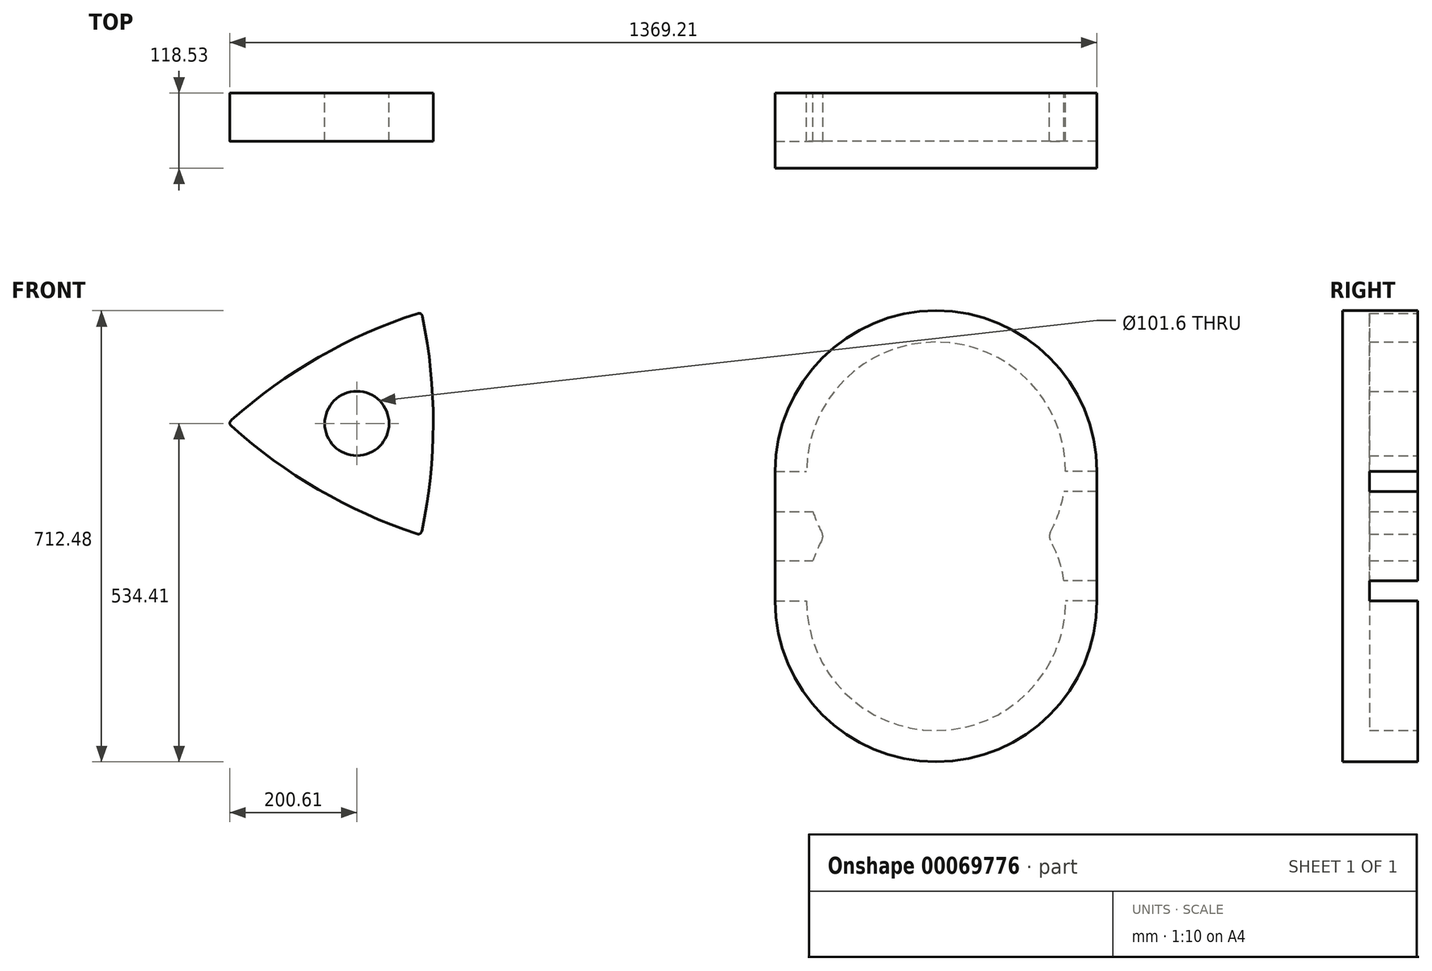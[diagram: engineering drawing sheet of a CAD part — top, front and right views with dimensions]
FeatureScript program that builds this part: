
annotation { "Feature Type Name" : "Feature", "Feature Type Description" : "" }
export const myFeature = defineFeature(function(context is Context, id is Id, definition is map)
    precondition{}
    {
        {
            var Q0;
            Q0=qCreatedBy(makeId("Front.planeOp"),FACE);
            var sketch = newSketch(context, id + "F0", { "sketchPlane" : qUnion([Q0])});
            skCircle(sketch, "E0", {"center": v(914.6, -75.93) * mm, "radius": 204.48 * mm});
            skCircle(sketch, "E1", {"center": v(914.6, -280.4) * mm, "radius": 204.48 * mm});
            skArc(sketch, "E2", {"start": v(1168.6, -75.93) * mm, "mid": v(914.6, 178.07) * mm, "end": v(660.6, -75.93) * mm});
            skLineSegment(sketch, "E3", {"start": v(660.6, -139.43) * mm, "end": v(660.6, -216.9) * mm});
            skArc(sketch, "E4", {"start": v(660.6, -280.4) * mm, "mid": v(914.6, -534.4) * mm, "end": v(1168.6, -280.4) * mm});
            skLineSegment(sketch, "E5", {"start": v(660.6, -75.93) * mm, "end": v(710.13, -75.93) * mm});
            skLineSegment(sketch, "E6", {"start": v(660.6, -139.43) * mm, "end": v(720.24, -139.43) * mm});
            skLineSegment(sketch, "E7", {"start": v(660.6, -216.9) * mm, "end": v(720.24, -216.9) * mm});
            skLineSegment(sketch, "E8", {"start": v(660.6, -280.4) * mm, "end": v(710.13, -280.4) * mm});
            skLineSegment(sketch, "E9", {"start": v(1168.6, -107.68) * mm, "end": v(1168.6, -248.66) * mm});
            skLineSegment(sketch, "E10", {"start": v(1168.6, -75.93) * mm, "end": v(1119.08, -75.93) * mm});
            skLineSegment(sketch, "E11", {"start": v(1168.6, -107.68) * mm, "end": v(1116.6, -107.68) * mm});
            skLineSegment(sketch, "E12", {"start": v(1168.6, -248.66) * mm, "end": v(1116.6, -248.66) * mm});
            skLineSegment(sketch, "E13", {"start": v(1168.6, -280.4) * mm, "end": v(1119.08, -280.4) * mm});
            skPoint(sketch, "E14", {"position": v(1091.69, -178.17) * mm});
            skPoint(sketch, "E15", {"position": v(737.52, -178.17) * mm});
            skSolve(sketch);
        }
        {
            var Q0;
            Q0=makeQuery(id+"F0.imprint","IMPRINT",FACE,{"disambiguationData":[TD([[makeQuery(id+"F0.imprint","IMPRINT",EDGE,{"derivedFrom":sQuery(id+"F0.wireOp",EDGE,"E2")}),1.0]])]});
            var Q1;
            Q1=makeQuery(id+"F0.imprint","IMPRINT",FACE,{"disambiguationData":[TD([[makeQuery(id+"F0.imprint","IMPRINT",EDGE,{"derivedFrom":sQuery(id+"F0.wireOp",EDGE,"E9")}),-1.0]])]});
            var Q2;
            Q2=makeQuery(id+"F0.imprint","IMPRINT",FACE,{"disambiguationData":[TD([[makeQuery(id+"F0.imprint","IMPRINT",EDGE,{"derivedFrom":sQuery(id+"F0.wireOp",EDGE,"E3")}),1.0]])]});
            var Q3;
            Q3=makeQuery(id+"F0.imprint","IMPRINT",FACE,{"disambiguationData":[TD([[makeQuery(id+"F0.imprint","IMPRINT",EDGE,{"derivedFrom":sQuery(id+"F0.wireOp",EDGE,"E4")}),1.0]])]});
            extrude(context, id + "F1", {"entities" : qUnion([Q0, Q1, Q2, Q3]), "depth" : 76.2 * mm});
        }
        {
            var Q0;
            {var subQ0=sQuery(id+"F0.wireOp",EDGE,"E1");var subQ1=sQuery(id+"F0.wireOp",EDGE,"E0");Q0=makeQuery(id+"F1.opExtrude","SWEPT_EDGE",EDGE,{"disambiguationData":[OSD([subQ1,subQ0]),TDD([makeQuery(id+"F0.imprint","INTERSECT",VERTEX,{"disambiguationData":[OD(0.0)],"derivedFrom":[subQ1,subQ0]})])]});}
            var Q1;
            {var subQ0=sQuery(id+"F0.wireOp",EDGE,"E1");var subQ1=sQuery(id+"F0.wireOp",EDGE,"E0");Q1=makeQuery(id+"F1.opExtrude","SWEPT_EDGE",EDGE,{"disambiguationData":[OSD([subQ1,subQ0]),TDD([makeQuery(id+"F0.imprint","INTERSECT",VERTEX,{"disambiguationData":[OD(1.0)],"derivedFrom":[subQ1,subQ0]})])]});}
            fillet(context, id + "F2", {"entities" : qUnion([Q0, Q1]), "radius" : 12.7 * mm, "tangentPropagation" : true, "allowEdgeOverflow" : false});
        }
        {
            var Q0;
            Q0=makeQuery(id+"F1.opExtrude","CAP_FACE",FACE,{"disambiguationData":[OSD([sQuery(id+"F0.wireOp",EDGE,"E0"),sQuery(id+"F0.wireOp",EDGE,"E2"),sQuery(id+"F0.wireOp",EDGE,"E5"),sQuery(id+"F0.wireOp",EDGE,"E10")])],"isStart":false});
            var sketch = newSketch(context, id + "F3", { "sketchPlane" : qUnion([Q0])});
            skArc(sketch, "E16", {"start": v(1168.6, -75.93) * mm, "mid": v(914.6, 178.07) * mm, "end": v(660.6, -75.93) * mm});
            skLineSegment(sketch, "E17", {"start": v(660.6, -75.93) * mm, "end": v(660.6, -280.4) * mm});
            skLineSegment(sketch, "E18", {"start": v(1168.6, -75.93) * mm, "end": v(1168.6, -280.4) * mm});
            skArc(sketch, "E19", {"start": v(660.6, -280.4) * mm, "mid": v(914.6, -534.4) * mm, "end": v(1168.6, -280.4) * mm});
            skSolve(sketch);
        }
        {
            var Q0;
            Q0 = qSketchRegion(id + "F3", true);
            extrude(context, id + "F4", {"entities" : qUnion([Q0]), "operationType" : NewBodyOperationType.ADD, "depth" : 42.33 * mm});
        }
        {
            var Q0;
            Q0=qCreatedBy(makeId("Front.planeOp"),FACE);
            var sketch = newSketch(context, id + "F5", { "sketchPlane" : qUnion([Q0])});
            skCircle(sketch, "E20.cCircle", {"center": v(0, 0) * mm, "radius": 101.6 * mm, "construction": true});
            skLineSegment(sketch, "E20.0", {"start": v(-203.2, 0.6) * mm, "end": v(102.12, 175.67) * mm});
            skLineSegment(sketch, "E20.1", {"start": v(102.12, 175.67) * mm, "end": v(101.08, -176.28) * mm});
            skLineSegment(sketch, "E20.2", {"start": v(101.08, -176.28) * mm, "end": v(-203.2, 0.6) * mm});
            skPoint(sketch, "E20.0.midPoint", {"position": v(-50.54, 88.14) * mm});
            skArc(sketch, "E21", {"start": v(101.08, -176.28) * mm, "mid": v(120.65, -0.36) * mm, "end": v(102.12, 175.67) * mm});
            skArc(sketch, "E22", {"start": v(-203.2, 0.6) * mm, "mid": v(-60.64, -104.3) * mm, "end": v(101.08, -176.28) * mm});
            skArc(sketch, "E23", {"start": v(102.12, 175.67) * mm, "mid": v(-60.01, 104.67) * mm, "end": v(-203.2, 0.6) * mm});
            skCircle(sketch, "E24", {"center": v(0, 0) * mm, "radius": 50.8 * mm});
            skSolve(sketch);
        }
        {
            var Q0;
            Q0 = qSketchRegion(id + "F5", true);
            extrude(context, id + "F6", {"entities" : qUnion([Q0]), "depth" : 76.2 * mm});
        }
        {
            var Q0;
            Q0=makeQuery(id+"F6.opExtrude","SWEPT_EDGE",EDGE,{"disambiguationData":[OSD([sQuery(id+"F5.wireOp",EDGE,"E20.0"),sQuery(id+"F5.wireOp",EDGE,"E20.1"),sQuery(id+"F5.wireOp",EDGE,"E21"),sQuery(id+"F5.wireOp",EDGE,"E23")])]});
            var Q1;
            Q1=makeQuery(id+"F6.opExtrude","SWEPT_EDGE",EDGE,{"disambiguationData":[OSD([sQuery(id+"F5.wireOp",EDGE,"E20.1"),sQuery(id+"F5.wireOp",EDGE,"E20.2"),sQuery(id+"F5.wireOp",EDGE,"E21"),sQuery(id+"F5.wireOp",EDGE,"E22")])]});
            var Q2;
            Q2=makeQuery(id+"F6.opExtrude","SWEPT_EDGE",EDGE,{"disambiguationData":[OSD([sQuery(id+"F5.wireOp",EDGE,"E20.0"),sQuery(id+"F5.wireOp",EDGE,"E20.2"),sQuery(id+"F5.wireOp",EDGE,"E22"),sQuery(id+"F5.wireOp",EDGE,"E23")])]});
            fillet(context, id + "F7", {"entities" : qUnion([Q0, Q1, Q2]), "radius" : 6.35 * mm, "tangentPropagation" : true, "rho" : 0.5, "crossSection" : FilletCrossSection.CONIC, "allowEdgeOverflow" : false});
        }
    });
